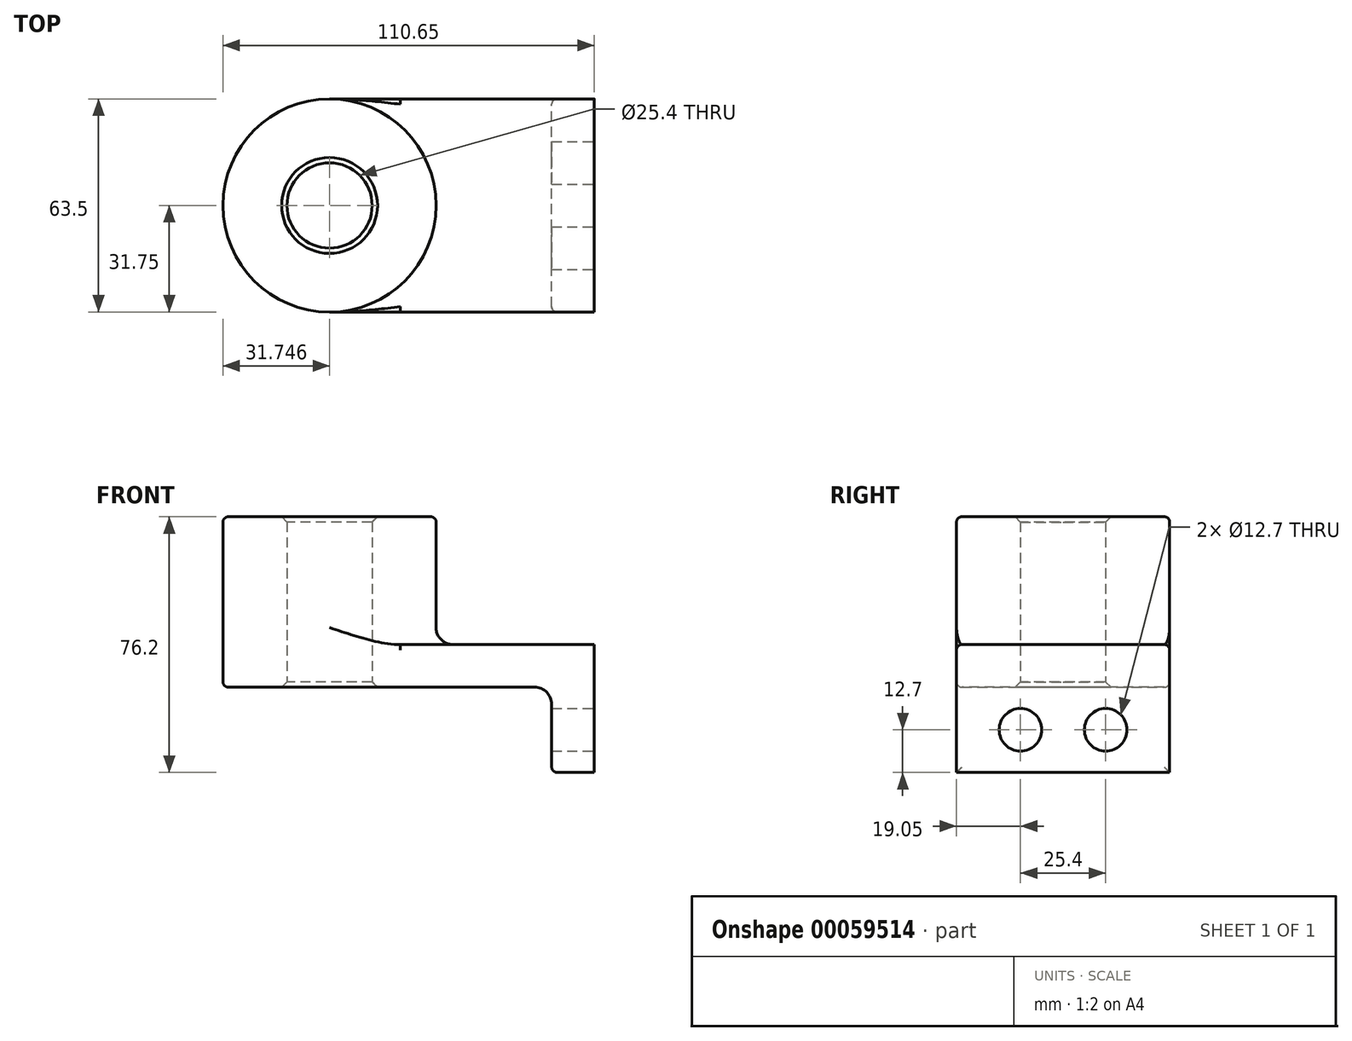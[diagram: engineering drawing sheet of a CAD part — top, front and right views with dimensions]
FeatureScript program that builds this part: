
annotation { "Feature Type Name" : "Feature", "Feature Type Description" : "" }
export const myFeature = defineFeature(function(context is Context, id is Id, definition is map)
    precondition{}
    {
        {
            var Q0;
            Q0=qCreatedBy(makeId("Top.planeOp"),FACE);
            var sketch = newSketch(context, id + "F0", { "sketchPlane" : qUnion([Q0])});
            skLineSegment(sketch, "E0.rect.bottom", {"start": v(-39.45, 31.75) * mm, "end": v(39.45, 31.75) * mm});
            skLineSegment(sketch, "E0.rect.top", {"start": v(-39.45, -31.75) * mm, "end": v(39.45, -31.75) * mm});
            skLineSegment(sketch, "E0.rect.left", {"start": v(-39.45, 31.75) * mm, "end": v(-39.45, -31.75) * mm});
            skLineSegment(sketch, "E0.rect.right", {"start": v(39.45, 31.75) * mm, "end": v(39.45, -31.75) * mm});
            skPoint(sketch, "E0.rect.middle", {"position": v(0, 0) * mm});
            skCircle(sketch, "E1", {"center": v(-39.45, 0) * mm, "radius": 31.75 * mm});
            skCircle(sketch, "E2", {"center": v(-39.45, 0) * mm, "radius": 12.7 * mm});
            skSolve(sketch);
        }
        {
            var Q0;
            Q0 = qSketchRegion(id + "F0", true);
            extrude(context, id + "F1", {"entities" : qUnion([Q0]), "depth" : 12.7 * mm});
        }
        {
            var Q0;
            {var subQ1=sQuery(id+"F0.wireOp",EDGE,"E0.rect.left");var subQ3=sQuery(id+"F0.wireOp",EDGE,"E2");var subQ4=makeQuery(id+"F0.imprint","INTERSECT",VERTEX,{"disambiguationData":[OD(0.0)],"derivedFrom":[subQ1,subQ3]});Q0=makeQuery(id+"F0.imprint","IMPRINT",FACE,{"disambiguationData":[TD([[makeQuery(id+"F0.imprint","IMPRINT",EDGE,{"disambiguationData":[TD([[subQ4,-1.0]])],"derivedFrom":subQ3}),-1.0]])]});}
            var Q1;
            {var subQ1=sQuery(id+"F0.wireOp",EDGE,"E0.rect.left");var subQ3=sQuery(id+"F0.wireOp",EDGE,"E2");var subQ4=makeQuery(id+"F0.imprint","INTERSECT",VERTEX,{"disambiguationData":[OD(0.0)],"derivedFrom":[subQ1,subQ3]});Q1=makeQuery(id+"F0.imprint","IMPRINT",FACE,{"disambiguationData":[TD([[makeQuery(id+"F0.imprint","IMPRINT",EDGE,{"disambiguationData":[TD([[subQ4,1.0]])],"derivedFrom":subQ3}),-1.0]])]});}
            extrude(context, id + "F2", {"entities" : qUnion([Q0, Q1]), "operationType" : NewBodyOperationType.ADD, "depth" : 50.8 * mm});
        }
        {
            var Q0;
            Q0=makeQuery(id+"F1.opExtrude","SWEPT_FACE",FACE,{"disambiguationData":[OSD([sQuery(id+"F0.wireOp",EDGE,"E0.rect.right")])]});
            var sketch = newSketch(context, id + "F3", { "sketchPlane" : qUnion([Q0])});
            skLineSegment(sketch, "E3.bottom", {"start": v(-31.75, 12.7) * mm, "end": v(31.75, 12.7) * mm});
            skLineSegment(sketch, "E3.top", {"start": v(-31.75, -25.4) * mm, "end": v(31.75, -25.4) * mm});
            skLineSegment(sketch, "E3.left", {"start": v(-31.75, 12.7) * mm, "end": v(-31.75, -25.4) * mm});
            skLineSegment(sketch, "E3.right", {"start": v(31.75, 12.7) * mm, "end": v(31.75, -25.4) * mm});
            skCircle(sketch, "E4", {"center": v(-12.7, -12.7) * mm, "radius": 6.35 * mm});
            skLineSegment(sketch, "E5", {"start": v(0, -1.58) * mm, "end": v(0, -25.4) * mm, "construction": true});
            skCircle(sketch, "E6.MirrorC", {"center": v(12.7, -12.7) * mm, "radius": 6.35 * mm});
            skSolve(sketch);
        }
        {
            var Q0;
            Q0 = qSketchRegion(id + "F3", true);
            extrude(context, id + "F4", {"entities" : qUnion([Q0]), "operationType" : NewBodyOperationType.ADD, "oppositeDirection" : true, "depth" : 12.7 * mm});
        }
        {
            var Q0;
            {var subQ0=sQuery(id+"F0.wireOp",EDGE,"E1");Q0=makeQuery(id+"F2.boolean.opBoolean","INTERSECT",EDGE,{"derivedFrom":[makeQuery(id+"F1.opExtrude","CAP_FACE",FACE,{"disambiguationData":[OSD([sQuery(id+"F0.wireOp",EDGE,"E0.rect.bottom"),sQuery(id+"F0.wireOp",EDGE,"E0.rect.top"),sQuery(id+"F0.wireOp",EDGE,"E0.rect.right"),subQ0,sQuery(id+"F0.wireOp",EDGE,"E2")])],"isStart":false}),makeQuery(id+"F2.opExtrude","SWEPT_FACE",FACE,{"disambiguationData":[OSD([subQ0])]})]});}
            fillet(context, id + "F5", {"entities" : qUnion([Q0]), "radius" : 5.08 * mm, "tangentPropagation" : true, "allowEdgeOverflow" : false});
        }
        {
            var Q0;
            Q0=makeQuery(id+"F4.boolean.opBoolean","INTERSECT",EDGE,{"derivedFrom":[makeQuery(id+"F1.opExtrude","CAP_FACE",FACE,{"disambiguationData":[OSD([sQuery(id+"F0.wireOp",EDGE,"E0.rect.bottom"),sQuery(id+"F0.wireOp",EDGE,"E0.rect.top"),sQuery(id+"F0.wireOp",EDGE,"E0.rect.right"),sQuery(id+"F0.wireOp",EDGE,"E1"),sQuery(id+"F0.wireOp",EDGE,"E2")])],"isStart":true}),makeQuery(id+"F4.opExtrude","CAP_FACE",FACE,{"disambiguationData":[OSD([sQuery(id+"F3.wireOp",EDGE,"E3.bottom"),sQuery(id+"F3.wireOp",EDGE,"E3.top"),sQuery(id+"F3.wireOp",EDGE,"E3.left"),sQuery(id+"F3.wireOp",EDGE,"E3.right"),sQuery(id+"F3.wireOp",EDGE,"E4"),sQuery(id+"F3.wireOp",EDGE,"E6.MirrorC")])],"isStart":false})]});
            fillet(context, id + "F6", {"entities" : qUnion([Q0]), "radius" : 5.08 * mm, "tangentPropagation" : true, "allowEdgeOverflow" : false});
        }
        {
            var Q0;
            Q0=makeQuery(id+"F4.opExtrude","CAP_EDGE",EDGE,{"disambiguationData":[OSD([sQuery(id+"F3.wireOp",EDGE,"E3.right")])],"isStart":false});
            var Q1;
            Q1=makeQuery(id+"F4.opExtrude","CAP_EDGE",EDGE,{"disambiguationData":[OSD([sQuery(id+"F3.wireOp",EDGE,"E3.top")])],"isStart":false});
            var Q2;
            Q2=makeQuery(id+"F1.opExtrude","CAP_EDGE",EDGE,{"disambiguationData":[OSD([sQuery(id+"F0.wireOp",EDGE,"E0.rect.top")])],"isStart":false});
            fillet(context, id + "F7", {"entities" : qUnion([Q0, Q1, Q2]), "radius" : 1.59 * mm, "tangentPropagation" : true, "allowEdgeOverflow" : false});
        }
        {
            var Q0;
            Q0=makeQuery(id+"F1.opExtrude","CAP_EDGE",EDGE,{"disambiguationData":[OSD([sQuery(id+"F0.wireOp",EDGE,"E0.rect.bottom")])],"isStart":false});
            fillet(context, id + "F8", {"entities" : qUnion([Q0]), "radius" : 1.59 * mm, "tangentPropagation" : true, "allowEdgeOverflow" : false});
        }
        {
            var Q0;
            {var subQ0=sQuery(id+"F0.wireOp",EDGE,"E2");Q0=makeQuery(id+"F2.boolean.opBoolean","MERGE",FACE,{"derivedFrom":[makeQuery(id+"F1.opExtrude","SWEPT_FACE",FACE,{"disambiguationData":[OSD([subQ0])]}),makeQuery(id+"F2.opExtrude","SWEPT_FACE",FACE,{"disambiguationData":[OSD([subQ0])]})]});}
            chamfer(context, id + "F9", {"entities" : qUnion([Q0]), "width" : 1.59 * mm, "tangentPropagation" : true});
        }
        {
            var Q0;
            Q0=makeQuery(id+"F2.opExtrude","CAP_EDGE",EDGE,{"disambiguationData":[OSD([sQuery(id+"F0.wireOp",EDGE,"E1")])],"isStart":false});
            fillet(context, id + "F10", {"entities" : qUnion([Q0]), "radius" : 1.59 * mm, "tangentPropagation" : true, "allowEdgeOverflow" : false});
        }
    });
